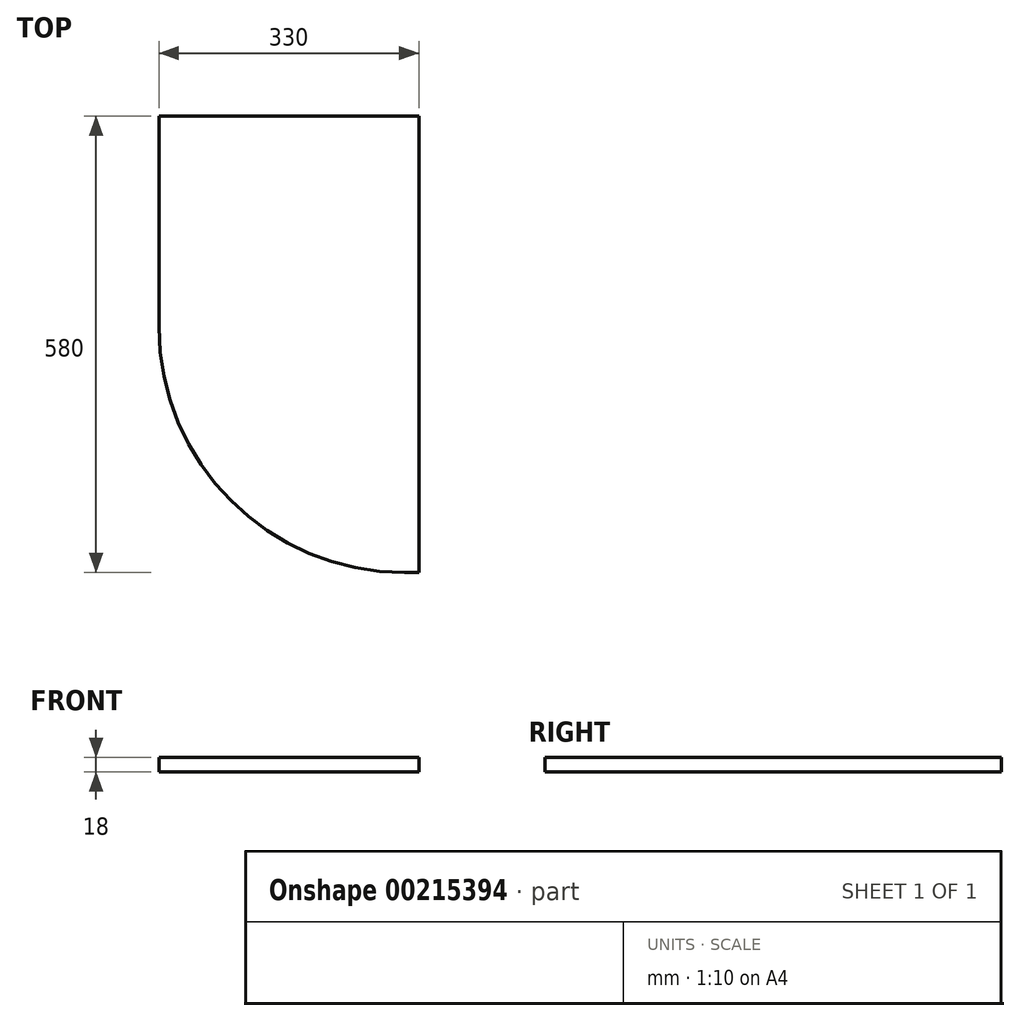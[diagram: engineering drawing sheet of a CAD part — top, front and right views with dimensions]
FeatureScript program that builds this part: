
annotation { "Feature Type Name" : "Feature", "Feature Type Description" : "" }
export const myFeature = defineFeature(function(context is Context, id is Id, definition is map)
    precondition{}
    {
        {
            var Q0;
            Q0=qCreatedBy(makeId("Top.planeOp"),FACE);
            var sketch = newSketch(context, id + "F0", { "sketchPlane" : qUnion([Q0])});
            skLineSegment(sketch, "E0", {"start": v(0, 0) * mm, "end": v(0, 580) * mm});
            skLineSegment(sketch, "E1", {"start": v(0, 580) * mm, "end": v(-330, 580) * mm});
            skLineSegment(sketch, "E2", {"start": v(0, 0) * mm, "end": v(-18, 0) * mm});
            skLineSegment(sketch, "E3", {"start": v(-330, 580) * mm, "end": v(-330, 312) * mm});
            skArc(sketch, "E4", {"start": v(-330, 312) * mm, "mid": v(-238.62, 91.38) * mm, "end": v(-18, 0) * mm});
            skSolve(sketch);
        }
        {
            var Q0;
            Q0=qSketchRegion(id+"F0",true);
            extrude(context, id + "F1", {"entities" : qUnion([Q0]), "depth" : 18 * mm});
        }
    });
